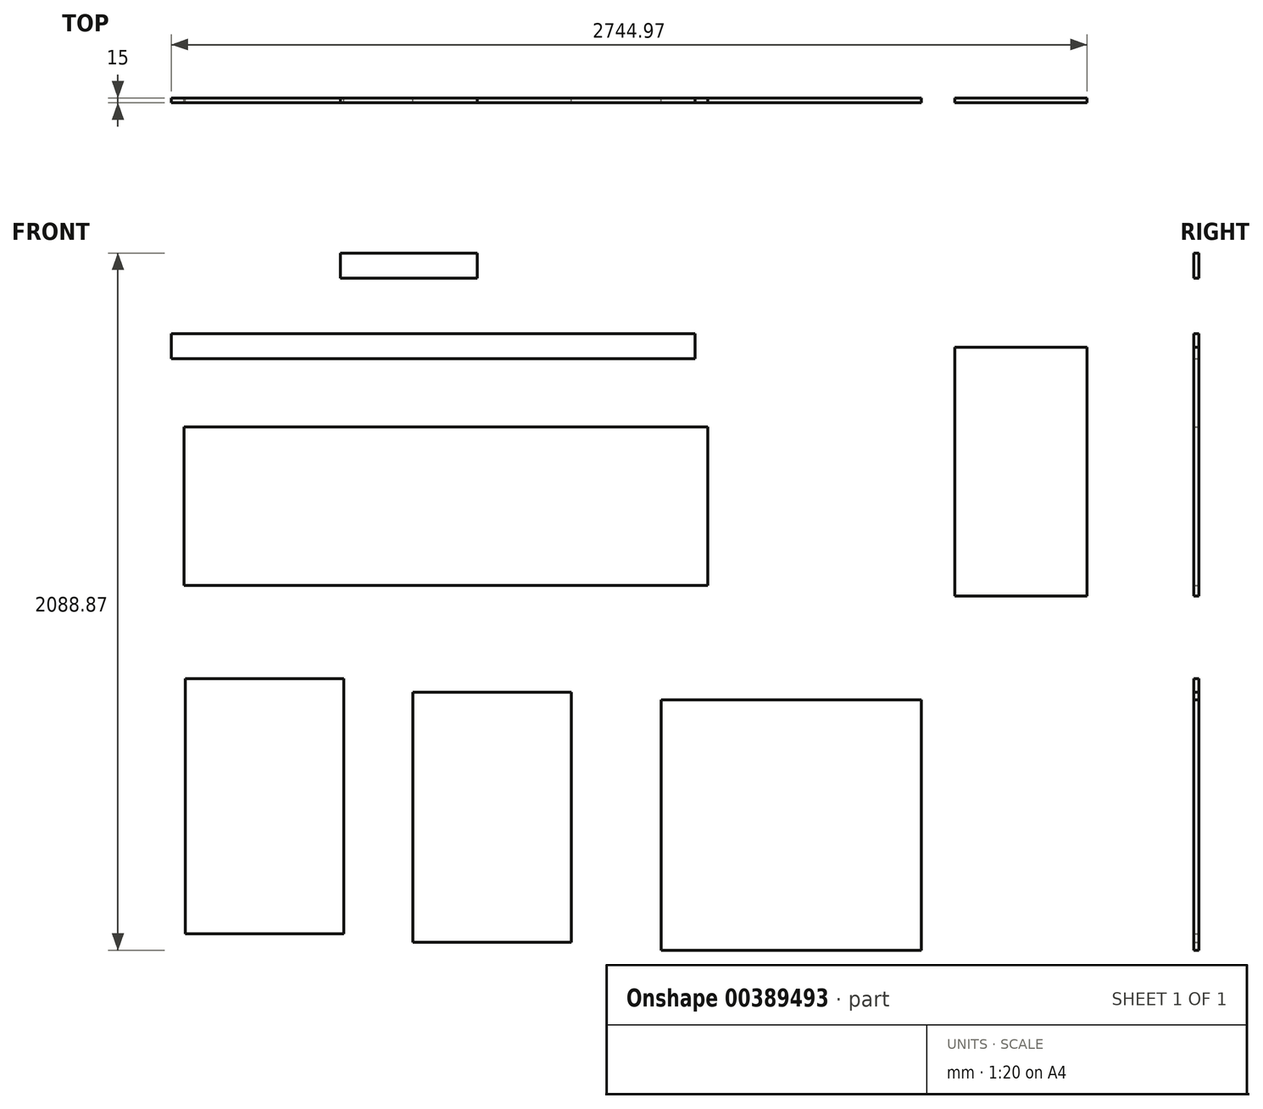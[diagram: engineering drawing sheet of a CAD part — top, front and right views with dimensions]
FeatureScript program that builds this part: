
annotation { "Feature Type Name" : "Feature", "Feature Type Description" : "" }
export const myFeature = defineFeature(function(context is Context, id is Id, definition is map)
    precondition{}
    {
        {
            var Q0;
            Q0=qCreatedBy(makeId("Front.planeOp"),FACE);
            var sketch = newSketch(context, id + "F0", { "sketchPlane" : qUnion([Q0])});
            skLineSegment(sketch, "E0.bottom", {"start": v(-1203.69, 66.22) * mm, "end": v(366.31, 66.22) * mm});
            skLineSegment(sketch, "E0.top", {"start": v(-1203.69, -8.78) * mm, "end": v(366.31, -8.78) * mm});
            skLineSegment(sketch, "E0.left", {"start": v(-1203.69, 66.22) * mm, "end": v(-1203.69, -8.78) * mm});
            skLineSegment(sketch, "E0.right", {"start": v(366.31, 66.22) * mm, "end": v(366.31, -8.78) * mm});
            skSolve(sketch);
        }
        {
            var Q0;
            Q0=makeQuery(id+"F0.imprint","IMPRINT",FACE,{"disambiguationData":[TD([[makeQuery(id+"F0.imprint","IMPRINT",EDGE,{"derivedFrom":sQuery(id+"F0.wireOp",EDGE,"E0.bottom")}),-1.0]])]});
            extrude(context, id + "F1", {"entities" : qUnion([Q0]), "depth" : 15 * mm, "offsetDistance" : 25 * mm});
        }
        {
            var Q0;
            Q0=qCreatedBy(makeId("Front.planeOp"),FACE);
            var sketch = newSketch(context, id + "F2", { "sketchPlane" : qUnion([Q0])});
            skLineSegment(sketch, "E1.bottom", {"start": v(-1166.23, -212.69) * mm, "end": v(403.77, -212.69) * mm});
            skLineSegment(sketch, "E1.top", {"start": v(-1166.23, -687.69) * mm, "end": v(403.77, -687.69) * mm});
            skLineSegment(sketch, "E1.left", {"start": v(-1166.23, -212.69) * mm, "end": v(-1166.23, -687.69) * mm});
            skLineSegment(sketch, "E1.right", {"start": v(403.77, -212.69) * mm, "end": v(403.77, -687.69) * mm});
            skSolve(sketch);
        }
        {
            var Q0;
            Q0=makeQuery(id+"F2.imprint","IMPRINT",FACE,{"disambiguationData":[TD([[makeQuery(id+"F2.imprint","IMPRINT",EDGE,{"derivedFrom":sQuery(id+"F2.wireOp",EDGE,"E1.bottom")}),-1.0]])]});
            extrude(context, id + "F3", {"entities" : qUnion([Q0]), "depth" : 15 * mm, "offsetDistance" : 25 * mm});
        }
        {
            var Q0;
            Q0=qCreatedBy(makeId("Front.planeOp"),FACE);
            var sketch = newSketch(context, id + "F4", { "sketchPlane" : qUnion([Q0])});
            skLineSegment(sketch, "E2.bottom", {"start": v(-1161.54, -967.1) * mm, "end": v(-686.54, -967.1) * mm});
            skLineSegment(sketch, "E2.top", {"start": v(-1161.54, -1732.1) * mm, "end": v(-686.54, -1732.1) * mm});
            skLineSegment(sketch, "E2.left", {"start": v(-1161.54, -967.1) * mm, "end": v(-1161.54, -1732.1) * mm});
            skLineSegment(sketch, "E2.right", {"start": v(-686.54, -967.1) * mm, "end": v(-686.54, -1732.1) * mm});
            skSolve(sketch);
        }
        {
            var Q0;
            Q0=makeQuery(id+"F4.imprint","IMPRINT",FACE,{"disambiguationData":[TD([[makeQuery(id+"F4.imprint","IMPRINT",EDGE,{"derivedFrom":sQuery(id+"F4.wireOp",EDGE,"E2.bottom")}),-1.0]])]});
            extrude(context, id + "F5", {"entities" : qUnion([Q0]), "depth" : 15 * mm, "offsetDistance" : 25 * mm});
        }
        {
            var Q0;
            Q0=qCreatedBy(makeId("Front.planeOp"),FACE);
            var sketch = newSketch(context, id + "F6", { "sketchPlane" : qUnion([Q0])});
            skLineSegment(sketch, "E3.bottom", {"start": v(-696.69, 307.92) * mm, "end": v(-286.69, 307.92) * mm});
            skLineSegment(sketch, "E3.top", {"start": v(-696.69, 232.92) * mm, "end": v(-286.69, 232.92) * mm});
            skLineSegment(sketch, "E3.left", {"start": v(-696.69, 307.92) * mm, "end": v(-696.69, 232.92) * mm});
            skLineSegment(sketch, "E3.right", {"start": v(-286.69, 307.92) * mm, "end": v(-286.69, 232.92) * mm});
            skSolve(sketch);
        }
        {
            var Q0;
            Q0=makeQuery(id+"F6.imprint","IMPRINT",FACE,{"disambiguationData":[TD([[makeQuery(id+"F6.imprint","IMPRINT",EDGE,{"derivedFrom":sQuery(id+"F6.wireOp",EDGE,"E3.bottom")}),-1.0]])]});
            extrude(context, id + "F7", {"entities" : qUnion([Q0]), "depth" : 15 * mm, "offsetDistance" : 25 * mm});
        }
        {
            var Q0;
            Q0=qCreatedBy(makeId("Front.planeOp"),FACE);
            var sketch = newSketch(context, id + "F8", { "sketchPlane" : qUnion([Q0])});
            skLineSegment(sketch, "E4.bottom", {"start": v(-480.11, -1007.79) * mm, "end": v(-5.11, -1007.79) * mm});
            skLineSegment(sketch, "E4.top", {"start": v(-480.11, -1757.79) * mm, "end": v(-5.11, -1757.79) * mm});
            skLineSegment(sketch, "E4.left", {"start": v(-480.11, -1007.79) * mm, "end": v(-480.11, -1757.79) * mm});
            skLineSegment(sketch, "E4.right", {"start": v(-5.11, -1007.79) * mm, "end": v(-5.11, -1757.79) * mm});
            skSolve(sketch);
        }
        {
            var Q0;
            Q0=makeQuery(id+"F8.imprint","IMPRINT",FACE,{"disambiguationData":[TD([[makeQuery(id+"F8.imprint","IMPRINT",EDGE,{"derivedFrom":sQuery(id+"F8.wireOp",EDGE,"E4.bottom")}),-1.0]])]});
            extrude(context, id + "F9", {"entities" : qUnion([Q0]), "depth" : 15 * mm, "offsetDistance" : 25 * mm});
        }
        {
            var Q0;
            Q0=qCreatedBy(makeId("Front.planeOp"),FACE);
            var sketch = newSketch(context, id + "F10", { "sketchPlane" : qUnion([Q0])});
            skLineSegment(sketch, "E5.bottom", {"start": v(264, -1030.95) * mm, "end": v(1044, -1030.95) * mm});
            skLineSegment(sketch, "E5.top", {"start": v(264, -1780.95) * mm, "end": v(1044, -1780.95) * mm});
            skLineSegment(sketch, "E5.left", {"start": v(264, -1030.95) * mm, "end": v(264, -1780.95) * mm});
            skLineSegment(sketch, "E5.right", {"start": v(1044, -1030.95) * mm, "end": v(1044, -1780.95) * mm});
            skSolve(sketch);
        }
        {
            var Q0;
            Q0=makeQuery(id+"F10.imprint","IMPRINT",FACE,{"disambiguationData":[TD([[makeQuery(id+"F10.imprint","IMPRINT",EDGE,{"derivedFrom":sQuery(id+"F10.wireOp",EDGE,"E5.bottom")}),-1.0]])]});
            extrude(context, id + "F11", {"entities" : qUnion([Q0]), "depth" : 15 * mm, "offsetDistance" : 25 * mm});
        }
        {
            var Q0;
            Q0=qCreatedBy(makeId("Front.planeOp"),FACE);
            var sketch = newSketch(context, id + "F12", { "sketchPlane" : qUnion([Q0])});
            skLineSegment(sketch, "E6.bottom", {"start": v(1144.28, 25.48) * mm, "end": v(1541.28, 25.48) * mm});
            skLineSegment(sketch, "E6.top", {"start": v(1144.28, -719.52) * mm, "end": v(1541.28, -719.52) * mm});
            skLineSegment(sketch, "E6.left", {"start": v(1144.28, 25.48) * mm, "end": v(1144.28, -719.52) * mm});
            skLineSegment(sketch, "E6.right", {"start": v(1541.28, 25.48) * mm, "end": v(1541.28, -719.52) * mm});
            skSolve(sketch);
        }
        {
            var Q0;
            Q0=makeQuery(id+"F12.imprint","IMPRINT",FACE,{"disambiguationData":[TD([[makeQuery(id+"F12.imprint","IMPRINT",EDGE,{"derivedFrom":sQuery(id+"F12.wireOp",EDGE,"E6.bottom")}),-1.0]])]});
            extrude(context, id + "F13", {"entities" : qUnion([Q0]), "depth" : 15 * mm, "offsetDistance" : 25 * mm});
        }
    });
